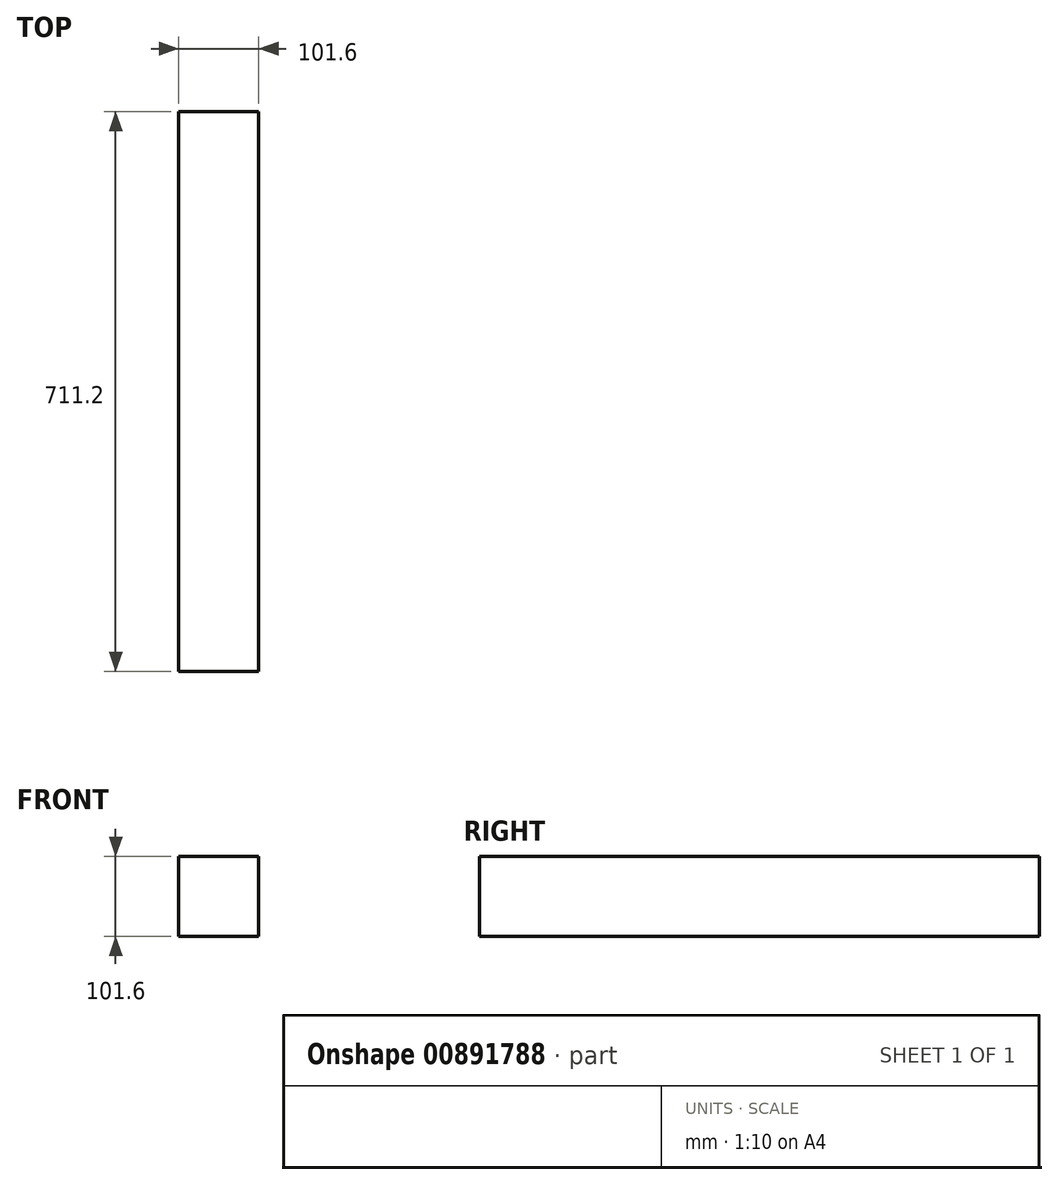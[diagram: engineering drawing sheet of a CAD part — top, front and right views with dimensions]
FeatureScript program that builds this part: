
annotation { "Feature Type Name" : "Feature", "Feature Type Description" : "" }
export const myFeature = defineFeature(function(context is Context, id is Id, definition is map)
    precondition{}
    {
        {
            var Q0;
            Q0=qCreatedBy(makeId("Front.planeOp"),FACE);
            var sketch = newSketch(context, id + "F0", { "sketchPlane" : qUnion([Q0])});
            skLineSegment(sketch, "E0.bottom", {"start": v(50.8, 50.8) * mm, "end": v(-50.8, 50.8) * mm});
            skLineSegment(sketch, "E0.top", {"start": v(50.8, -50.8) * mm, "end": v(-50.8, -50.8) * mm});
            skLineSegment(sketch, "E0.left", {"start": v(50.8, 50.8) * mm, "end": v(50.8, -50.8) * mm});
            skLineSegment(sketch, "E0.right", {"start": v(-50.8, 50.8) * mm, "end": v(-50.8, -50.8) * mm});
            skPoint(sketch, "E0.middle", {"position": v(0, 0) * mm});
            skSolve(sketch);
        }
        {
            var Q0;
            Q0=qSketchRegion(id+"F0",true);
            extrude(context, id + "F1", {"entities" : qUnion([Q0]), "depth" : 711.2 * mm});
        }
    });
